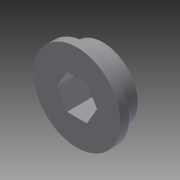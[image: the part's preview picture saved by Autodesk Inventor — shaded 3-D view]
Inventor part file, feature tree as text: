
AUTODESK INVENTOR PART (.ipt)
format: ipt  version: 2014 SP1 (Build 180222100, 222)  size: 97,792 bytes
history: native  units: in
note: dims shown in document units (in); Inventor stores cm internally (conversion verified against a paired STEP export)
features: extrude x4, sketch x4
ambient origin geometry x8: Origin, YZ Plane, XZ Plane, XY Plane, X Axis, Y Axis, Z Axis, Center Point
bodies: Solid1 (feature_tree)
feature tree (8):
  extrude  "Extrusion1"  Depth=0.25in TaperAngle=0.0deg
  extrude  "Extrusion2"  Depth=0.125in TaperAngle=0.0deg
  extrude  "Extrusion3"  Depth=0.5in
  extrude  "Extrusion4"  [1 undecoded]
  sketch  "Sketch1"  dims[d0=1.0in d1=0.25in d2=0.0in]
  sketch  "Sketch2"  dims[d3=1.25in d4=0.125in d5=0.0in]
  sketch  "Sketch3"  dims[d6=0.125in d7=0.0in d8=0.5in]
  sketch  "Sketch4"  dims[d9=0.125in d10=0.0in]
note: 1 required parameter value undecoded (feature->parameter linkage not recoverable at this tier; creation-order binding heuristic only, values carry confidence <= 0.55)
